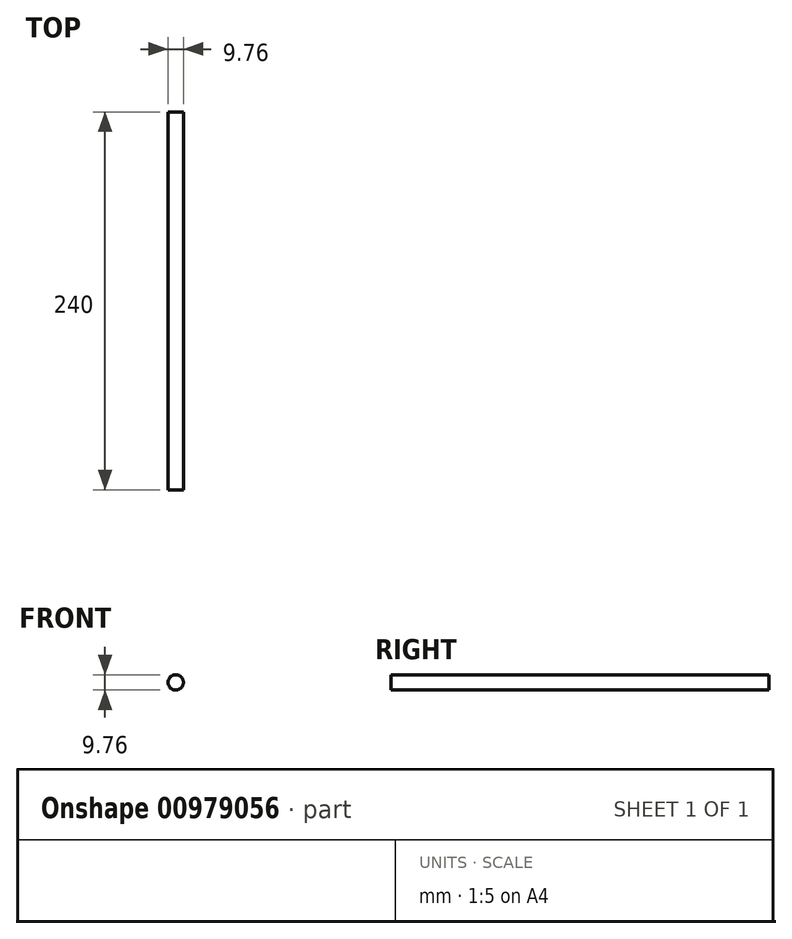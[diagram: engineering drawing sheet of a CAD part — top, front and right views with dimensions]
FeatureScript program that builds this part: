
annotation { "Feature Type Name" : "Feature", "Feature Type Description" : "" }
export const myFeature = defineFeature(function(context is Context, id is Id, definition is map)
    precondition{}
    {
        {
            var Q0;
            Q0=qCreatedBy(makeId("Front.planeOp"),FACE);
            var sketch = newSketch(context, id + "F0", { "sketchPlane" : qUnion([Q0])});
            skCircle(sketch, "E0", {"center": v(0, 0) * mm, "radius": 4.88 * mm});
            skSolve(sketch);
        }
        {
            var Q0;
            Q0=makeQuery(id+"F0.imprint","IMPRINT",FACE,{"disambiguationData":[TD([[makeQuery(id+"F0.imprint","IMPRINT",EDGE,{"derivedFrom":sQuery(id+"F0.wireOp",EDGE,"E0")}),1.0]])]});
            extrude(context, id + "F1", {"entities" : qUnion([Q0]), "depth" : 240 * mm, "offsetDistance" : 25 * mm});
        }
    });
